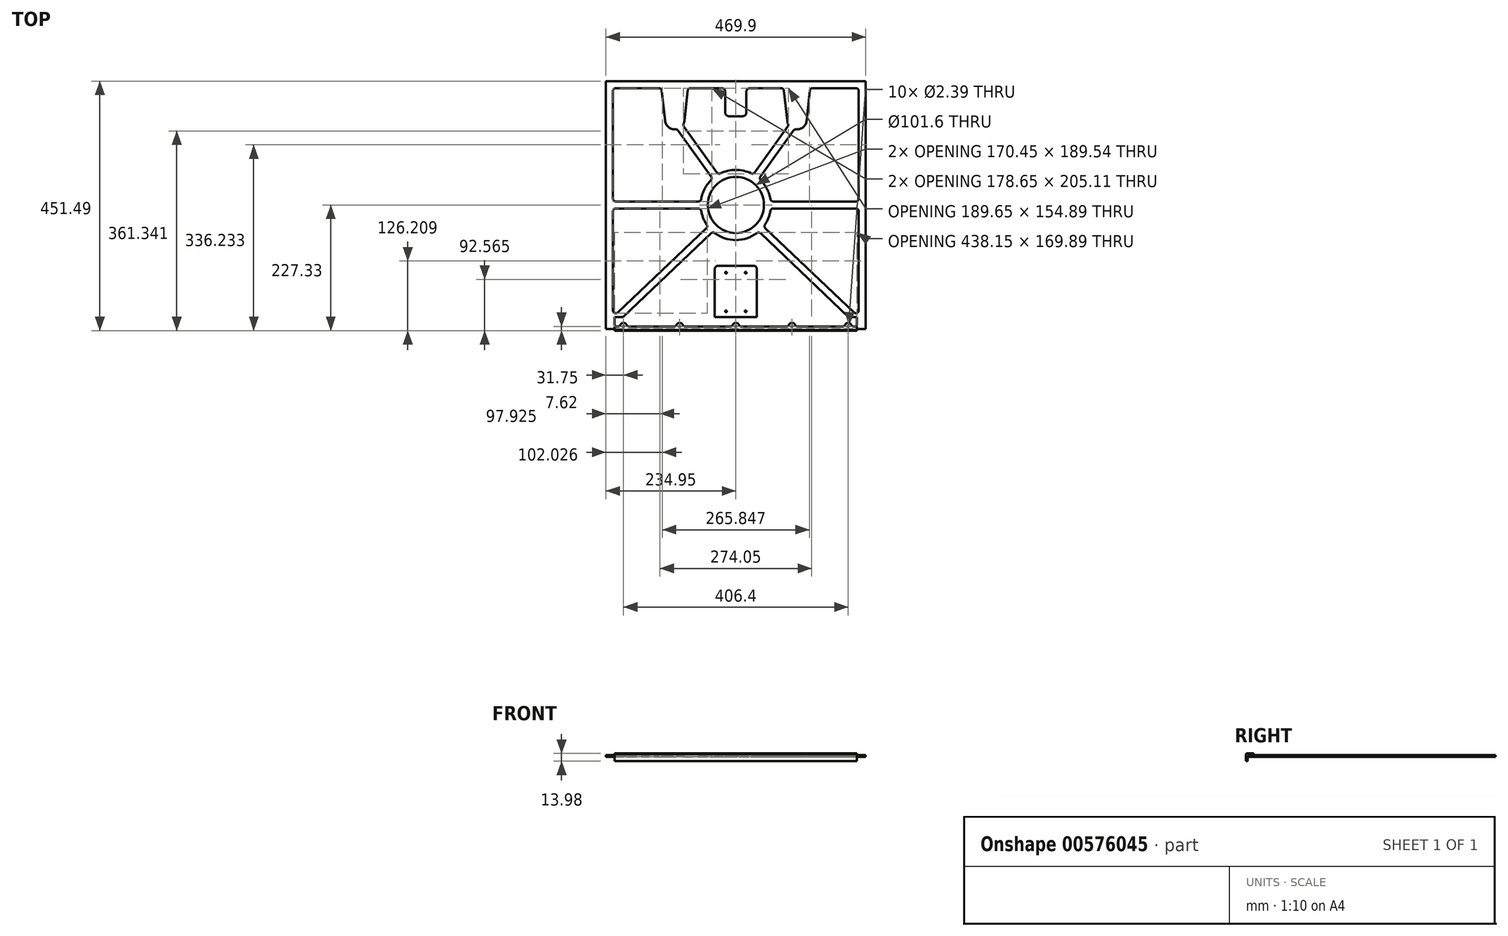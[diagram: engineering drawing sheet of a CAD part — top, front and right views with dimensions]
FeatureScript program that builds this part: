
annotation { "Feature Type Name" : "Feature", "Feature Type Description" : "" }
export const myFeature = defineFeature(function(context is Context, id is Id, definition is map)
    precondition{}
    {
        {
            var Q0;
            Q0=qCreatedBy(makeId("Top.planeOp"),FACE);
            cPlane(context, id + "F0", {"entities" : qUnion([Q0]), "cplaneType" : CPlaneType.OFFSET, "offset" : 3.17 * mm, "width" : 152.4 * mm, "height" : 152.4 * mm});
        }
        {
            var Q0;
            Q0=qCreatedBy(id+"F0.planeOp",FACE);
            var sketch = newSketch(context, id + "F1", { "sketchPlane" : qUnion([Q0])});
            skLineSegment(sketch, "E0.bottom", {"start": v(234.95, -224.15) * mm, "end": v(-234.95, -224.16) * mm});
            skLineSegment(sketch, "E0.top", {"start": v(234.95, 224.16) * mm, "end": v(-234.95, 224.15) * mm});
            skLineSegment(sketch, "E0.left", {"start": v(234.95, -224.15) * mm, "end": v(234.95, 224.16) * mm});
            skLineSegment(sketch, "E0.right", {"start": v(-234.95, -224.16) * mm, "end": v(-234.95, 224.15) * mm});
            skPoint(sketch, "E0.middle", {"position": v(0, 0) * mm});
            skSolve(sketch);
        }
        {
            var Q0;
            Q0=qSketchRegion(id+"F1",true);
            extrude(context, id + "F2", {"entities" : qUnion([Q0]), "depth" : 3.17 * mm, "offsetDistance" : 25.4 * mm});
        }
        {
            var Q0;
            Q0=makeQuery(id+"F2.opExtrude","CAP_FACE",FACE,{"disambiguationData":[OSD([sQuery(id+"F1.wireOp",EDGE,"E0.bottom"),sQuery(id+"F1.wireOp",EDGE,"E0.top"),sQuery(id+"F1.wireOp",EDGE,"E0.left"),sQuery(id+"F1.wireOp",EDGE,"E0.right")])],"isStart":false});
            var sketch = newSketch(context, id + "F3", { "sketchPlane" : qUnion([Q0])});
            skLineSegment(sketch, "E1", {"start": v(-234.95, -224.16) * mm, "end": v(-219.08, -224.16) * mm});
            skLineSegment(sketch, "E2", {"start": v(-219.08, -224.16) * mm, "end": v(-219.08, -249.56) * mm});
            skSolve(sketch);
        }
        {
            var Q0;
            Q0=sQuery(id+"F3.wireOp",EDGE,"E2");
            cPlane(context, id + "F4", {"entities" : qUnion([Q0]), "cplaneType" : CPlaneType.LINE_ANGLE, "offset" : 25.4 * mm, "angle" : 90 * degree, "width" : 152.4 * mm, "height" : 152.4 * mm});
        }
        {
            var Q0;
            Q0=qCreatedBy(id+"F4.planeOp",FACE);
            var sketch = newSketch(context, id + "F5", { "sketchPlane" : qUnion([Q0])});
            skLineSegment(sketch, "E3", {"start": v(-224.16, 6.35) * mm, "end": v(-224.16, 9.52) * mm});
            skLineSegment(sketch, "E4", {"start": v(-224.16, 9.52) * mm, "end": v(-227.33, 9.52) * mm});
            skLineSegment(sketch, "E5", {"start": v(-227.33, 9.52) * mm, "end": v(-208.28, 9.52) * mm});
            skLineSegment(sketch, "E6", {"start": v(-208.28, 9.52) * mm, "end": v(-208.28, 6.35) * mm});
            skLineSegment(sketch, "E7", {"start": v(-208.28, 6.35) * mm, "end": v(-224.16, 6.35) * mm});
            skLineSegment(sketch, "E8", {"start": v(-227.33, 9.52) * mm, "end": v(-227.33, -9.53) * mm});
            skLineSegment(sketch, "E9", {"start": v(-227.33, -9.53) * mm, "end": v(-224.16, -9.53) * mm});
            skLineSegment(sketch, "E10", {"start": v(-224.16, -9.53) * mm, "end": v(-224.16, 6.35) * mm});
            skSolve(sketch);
        }
        {
            var Q0;
            Q0=qSketchRegion(id+"F5",true);
            extrude(context, id + "F6", {"entities" : qUnion([Q0]), "depth" : 438.15 * mm, "offsetDistance" : 25.4 * mm});
        }
        {
            var Q0;
            {var subQ2=sQuery(id+"F3.wireOp",EDGE,"E1");Q0=makeQuery(id+"F3.imprint","IMPRINT",FACE,{"disambiguationData":[TD([[makeQuery(id+"F3.imprint","IMPRINT",EDGE,{"derivedFrom":subQ2}),-1.0]])]});}
            var sketch = newSketch(context, id + "F7", { "sketchPlane" : qUnion([Q0])});
            skLineSegment(sketch, "E11", {"start": v(-234.95, 224.15) * mm, "end": v(-110.5, 224.15) * mm});
            skLineSegment(sketch, "E12", {"start": v(-110.5, 224.15) * mm, "end": v(-110.5, 154.3) * mm});
            skArc(sketch, "E13", {"start": v(-121.74, 153.07) * mm, "mid": v(-110.49, 143) * mm, "end": v(-99.24, 153.07) * mm});
            skLineSegment(sketch, "E14", {"start": v(-110.5, 224.15) * mm, "end": v(-129.54, 224.15) * mm});
            skLineSegment(sketch, "E15", {"start": v(-129.54, 224.15) * mm, "end": v(-121.74, 153.07) * mm});
            skLineSegment(sketch, "E16.MirrorCS", {"start": v(-91.44, 224.15) * mm, "end": v(-99.24, 153.07) * mm});
            skLineSegment(sketch, "E17.MirrorCS", {"start": v(-110.5, 224.15) * mm, "end": v(-91.44, 224.15) * mm});
            skLineSegment(sketch, "E18", {"start": v(-91.44, 224.15) * mm, "end": v(0, 224.15) * mm});
            skLineSegment(sketch, "E19", {"start": v(0, 224.15) * mm, "end": v(0, 261.42) * mm});
            skLineSegment(sketch, "E20.MirrorCS", {"start": v(91.44, 224.15) * mm, "end": v(0, 224.15) * mm});
            skLineSegment(sketch, "E21.MirrorCS", {"start": v(110.5, 224.15) * mm, "end": v(91.44, 224.15) * mm});
            skLineSegment(sketch, "E22.MirrorCS", {"start": v(129.54, 224.15) * mm, "end": v(121.74, 153.07) * mm});
            skLineSegment(sketch, "E23.MirrorCS", {"start": v(91.44, 224.15) * mm, "end": v(99.24, 153.07) * mm});
            skLineSegment(sketch, "E24.MirrorCS", {"start": v(110.5, 224.15) * mm, "end": v(110.5, 154.3) * mm});
            skArc(sketch, "E25.MirrorCS", {"start": v(121.74, 153.07) * mm, "mid": v(110.49, 143) * mm, "end": v(99.24, 153.07) * mm});
            skLineSegment(sketch, "E26.MirrorCS", {"start": v(110.5, 224.15) * mm, "end": v(129.54, 224.15) * mm});
            skLineSegment(sketch, "E27.MirrorCS", {"start": v(234.95, 224.15) * mm, "end": v(110.5, 224.15) * mm});
            skLineSegment(sketch, "E28.bottom", {"start": v(-234.95, 224.15) * mm, "end": v(234.95, 224.15) * mm});
            skLineSegment(sketch, "E28.top", {"start": v(-234.95, -224.15) * mm, "end": v(234.95, -224.15) * mm});
            skLineSegment(sketch, "E28.left", {"start": v(-234.95, 224.15) * mm, "end": v(-234.95, -224.15) * mm});
            skLineSegment(sketch, "E28.right", {"start": v(234.95, 224.15) * mm, "end": v(234.95, -224.15) * mm});
            skLineSegment(sketch, "E29.0", {"start": v(-222.25, 206.37) * mm, "end": v(-222.25, 11.43) * mm});
            skLineSegment(sketch, "E29.1", {"start": v(-217.17, 211.45) * mm, "end": v(-139.09, 211.45) * mm});
            skLineSegment(sketch, "E29.2", {"start": v(222.25, -11.43) * mm, "end": v(222.25, -190.84) * mm});
            skLineSegment(sketch, "E29.3", {"start": v(-200.33, -211.45) * mm, "end": v(-44.45, -211.45) * mm});
            skLineSegment(sketch, "E30.0", {"start": v(-86.94, 206.93) * mm, "end": v(-92.93, 152.38) * mm});
            skArc(sketch, "E30.1", {"start": v(-128.05, 152.38) * mm, "mid": v(-121.64, 140.6) * mm, "end": v(-108.82, 136.72) * mm});
            skLineSegment(sketch, "E30.2", {"start": v(-134.04, 206.93) * mm, "end": v(-128.05, 152.38) * mm});
            skLineSegment(sketch, "E31.0", {"start": v(134.04, 206.93) * mm, "end": v(128.05, 152.38) * mm});
            skArc(sketch, "E31.1", {"start": v(128.05, 152.38) * mm, "mid": v(121.64, 140.6) * mm, "end": v(108.82, 136.72) * mm});
            skLineSegment(sketch, "E31.2", {"start": v(86.94, 206.93) * mm, "end": v(92.93, 152.38) * mm});
            skCircle(sketch, "E32", {"center": v(0, 0) * mm, "radius": 50.8 * mm});
            skArc(sketch, "E33.0", {"start": v(-62.61, -10.58) * mm, "mid": v(-58.96, -23.57) * mm, "end": v(-52.66, -35.5) * mm});
            skLineSegment(sketch, "E34.0", {"start": v(-34.2, 58.68) * mm, "end": v(-93.88, 142.01) * mm});
            skLineSegment(sketch, "E35.0", {"start": v(-44.61, -51.21) * mm, "end": v(-203.83, -202.7) * mm});
            skLineSegment(sketch, "E36.trimOffspring", {"start": v(-44.53, 51.28) * mm, "end": v(-104.2, 134.62) * mm});
            skLineSegment(sketch, "E37.trimOffspring", {"start": v(-67.62, 6.35) * mm, "end": v(-217.17, 6.35) * mm});
            skLineSegment(sketch, "E38.trimOffspring", {"start": v(-67.62, -6.35) * mm, "end": v(-217.17, -6.35) * mm});
            skLineSegment(sketch, "E39.trimOffspring", {"start": v(-53.37, -42.01) * mm, "end": v(-213.67, -194.53) * mm});
            skLineSegment(sketch, "E40.trimOffspring", {"start": v(-36.8, -35.02) * mm, "end": v(-222.25, -211.45) * mm});
            skLineSegment(sketch, "E41.trimOffspring", {"start": v(-50.8, 0) * mm, "end": v(-222.25, 0) * mm});
            skLineSegment(sketch, "E42.trimOffspring", {"start": v(-29.58, 41.3) * mm, "end": v(-103.9, 145.1) * mm});
            skLineSegment(sketch, "E43.MirrorCS", {"start": v(34.2, 58.68) * mm, "end": v(93.88, 142.01) * mm});
            skLineSegment(sketch, "E44.MirrorCS", {"start": v(29.58, 41.3) * mm, "end": v(103.9, 145.1) * mm});
            skLineSegment(sketch, "E45.MirrorCS", {"start": v(44.53, 51.28) * mm, "end": v(104.2, 134.62) * mm});
            skLineSegment(sketch, "E46.MirrorCS", {"start": v(67.62, 6.35) * mm, "end": v(217.17, 6.35) * mm});
            skLineSegment(sketch, "E47.MirrorCS", {"start": v(50.8, 0) * mm, "end": v(222.25, 0) * mm});
            skLineSegment(sketch, "E48.MirrorCS", {"start": v(67.62, -6.35) * mm, "end": v(217.17, -6.35) * mm});
            skLineSegment(sketch, "E49.MirrorCS", {"start": v(53.37, -42.01) * mm, "end": v(213.67, -194.53) * mm});
            skLineSegment(sketch, "E50.MirrorCS", {"start": v(36.8, -35.02) * mm, "end": v(222.25, -211.45) * mm});
            skLineSegment(sketch, "E51.MirrorCS", {"start": v(44.61, -51.21) * mm, "end": v(203.83, -202.7) * mm});
            skArc(sketch, "E52.filletArc", {"start": v(-134.04, 206.93) * mm, "mid": v(-135.7, 210.16) * mm, "end": v(-139.09, 211.45) * mm});
            skPoint(sketch, "E53.visualSharp", {"position": v(-222.25, 211.45) * mm});
            skArc(sketch, "E53.filletArc", {"start": v(-217.17, 211.45) * mm, "mid": v(-220.76, 209.97) * mm, "end": v(-222.25, 206.37) * mm});
            skPoint(sketch, "E54.newPointA", {"position": v(-222.25, -211.45) * mm});
            skPoint(sketch, "E54.newPointB", {"position": v(-222.25, 6.35) * mm});
            skArc(sketch, "E54.filletArc", {"start": v(-222.25, 11.43) * mm, "mid": v(-220.76, 7.84) * mm, "end": v(-217.17, 6.35) * mm});
            skLineSegment(sketch, "E55", {"start": v(217.17, 211.45) * mm, "end": v(139.09, 211.45) * mm});
            skLineSegment(sketch, "E56", {"start": v(-222.25, -11.43) * mm, "end": v(-222.25, -190.84) * mm});
            skArc(sketch, "E57.trimOffspring", {"start": v(-38.07, -50.83) * mm, "mid": v(0, -63.5) * mm, "end": v(38.07, -50.83) * mm});
            skArc(sketch, "E58.trimOffspring", {"start": v(52.66, -35.5) * mm, "mid": v(58.96, -23.57) * mm, "end": v(62.61, -10.58) * mm});
            skArc(sketch, "E59.trimOffspring", {"start": v(62.61, 10.58) * mm, "mid": v(56.48, 29.02) * mm, "end": v(45.06, 44.75) * mm});
            skArc(sketch, "E60.trimOffspring", {"start": v(27.85, 57.07) * mm, "mid": v(0, 63.5) * mm, "end": v(-27.85, 57.07) * mm});
            skArc(sketch, "E61.trimOffspring", {"start": v(-45.06, 44.75) * mm, "mid": v(-56.48, 29.02) * mm, "end": v(-62.61, 10.58) * mm});
            skPoint(sketch, "E62.orphan", {"position": v(-110.2, 143) * mm});
            skPoint(sketch, "E63.orphan", {"position": v(-99.88, 150.39) * mm});
            skArc(sketch, "E64.trimOffspring", {"start": v(-94.38, 147.06) * mm, "mid": v(-93.45, 149.66) * mm, "end": v(-92.93, 152.38) * mm});
            skPoint(sketch, "E65.orphan", {"position": v(99.88, 150.39) * mm});
            skPoint(sketch, "E66.orphan", {"position": v(110.2, 143) * mm});
            skArc(sketch, "E67.trimOffspring", {"start": v(94.38, 147.06) * mm, "mid": v(93.45, 149.66) * mm, "end": v(92.93, 152.38) * mm});
            skPoint(sketch, "E68.visualSharp", {"position": v(-106.06, 137.2) * mm});
            skArc(sketch, "E68.filletArc", {"start": v(-104.2, 134.62) * mm, "mid": v(-106.23, 136.29) * mm, "end": v(-108.82, 136.72) * mm});
            skPoint(sketch, "E69.newPointA", {"position": v(-34.5, 37.28) * mm});
            skArc(sketch, "E69.filletArc", {"start": v(-45.06, 44.75) * mm, "mid": v(-43.6, 47.92) * mm, "end": v(-44.53, 51.28) * mm});
            skPoint(sketch, "E70.newPointB", {"position": v(-50.4, 6.35) * mm});
            skArc(sketch, "E70.filletArc", {"start": v(-67.62, 6.35) * mm, "mid": v(-64.34, 7.55) * mm, "end": v(-62.61, 10.58) * mm});
            skPoint(sketch, "E71.newPointA", {"position": v(-50.4, -6.35) * mm});
            skArc(sketch, "E71.filletArc", {"start": v(-62.61, -10.58) * mm, "mid": v(-64.34, -7.55) * mm, "end": v(-67.62, -6.35) * mm});
            skPoint(sketch, "E72.newPointB", {"position": v(-40.9, -30.14) * mm});
            skArc(sketch, "E72.filletArc", {"start": v(-53.37, -42.01) * mm, "mid": v(-51.82, -38.88) * mm, "end": v(-52.66, -35.5) * mm});
            skPoint(sketch, "E73.newPointA", {"position": v(-222.25, -202.7) * mm});
            skArc(sketch, "E73.filletArc", {"start": v(-222.25, -190.84) * mm, "mid": v(-219.17, -195.51) * mm, "end": v(-213.67, -194.53) * mm});
            skPoint(sketch, "E74.visualSharp", {"position": v(-222.25, -6.35) * mm});
            skArc(sketch, "E74.filletArc", {"start": v(-217.17, -6.35) * mm, "mid": v(-220.76, -7.84) * mm, "end": v(-222.25, -11.43) * mm});
            skPoint(sketch, "E75.newPointB", {"position": v(-32.14, -39.34) * mm});
            skArc(sketch, "E75.filletArc", {"start": v(-38.07, -50.83) * mm, "mid": v(-41.41, -49.82) * mm, "end": v(-44.61, -51.21) * mm});
            skPoint(sketch, "E76.newPointB", {"position": v(32.14, -39.34) * mm});
            skArc(sketch, "E76.filletArc", {"start": v(44.61, -51.21) * mm, "mid": v(41.41, -49.82) * mm, "end": v(38.07, -50.83) * mm});
            skPoint(sketch, "E77.newPointA", {"position": v(213.04, -211.46) * mm});
            skArc(sketch, "E77.filletArc", {"start": v(200.33, -211.45) * mm, "mid": v(205.05, -208.26) * mm, "end": v(203.83, -202.7) * mm});
            skPoint(sketch, "E78.newPointB", {"position": v(-213.04, -211.46) * mm});
            skArc(sketch, "E78.filletArc", {"start": v(-203.83, -202.7) * mm, "mid": v(-205.05, -208.26) * mm, "end": v(-200.33, -211.46) * mm});
            skPoint(sketch, "E79.newPointA", {"position": v(222.25, -202.7) * mm});
            skArc(sketch, "E79.filletArc", {"start": v(213.67, -194.53) * mm, "mid": v(219.17, -195.51) * mm, "end": v(222.25, -190.84) * mm});
            skPoint(sketch, "E80.newPointB", {"position": v(222.25, -6.35) * mm});
            skArc(sketch, "E80.filletArc", {"start": v(222.25, -11.43) * mm, "mid": v(220.76, -7.84) * mm, "end": v(217.17, -6.35) * mm});
            skPoint(sketch, "E81.newPointA", {"position": v(50.4, -6.35) * mm});
            skArc(sketch, "E81.filletArc", {"start": v(67.62, -6.35) * mm, "mid": v(64.34, -7.55) * mm, "end": v(62.61, -10.58) * mm});
            skPoint(sketch, "E82.newPointA", {"position": v(40.9, -30.14) * mm});
            skArc(sketch, "E82.filletArc", {"start": v(52.66, -35.5) * mm, "mid": v(51.82, -38.88) * mm, "end": v(53.37, -42.01) * mm});
            skLineSegment(sketch, "E83", {"start": v(222.25, 206.37) * mm, "end": v(222.25, 11.43) * mm});
            skPoint(sketch, "E84.visualSharp", {"position": v(222.25, 6.35) * mm});
            skArc(sketch, "E84.filletArc", {"start": v(217.17, 6.35) * mm, "mid": v(220.76, 7.84) * mm, "end": v(222.25, 11.43) * mm});
            skPoint(sketch, "E85.visualSharp", {"position": v(222.25, 211.45) * mm});
            skArc(sketch, "E85.filletArc", {"start": v(222.25, 206.37) * mm, "mid": v(220.76, 209.97) * mm, "end": v(217.17, 211.45) * mm});
            skArc(sketch, "E86.filletArc", {"start": v(139.09, 211.45) * mm, "mid": v(135.7, 210.16) * mm, "end": v(134.04, 206.93) * mm});
            skPoint(sketch, "E87.visualSharp", {"position": v(106.06, 137.2) * mm});
            skArc(sketch, "E87.filletArc", {"start": v(108.82, 136.72) * mm, "mid": v(106.23, 136.29) * mm, "end": v(104.2, 134.62) * mm});
            skPoint(sketch, "E88.newPointA", {"position": v(34.5, 37.28) * mm});
            skArc(sketch, "E88.filletArc", {"start": v(44.53, 51.28) * mm, "mid": v(43.6, 47.92) * mm, "end": v(45.06, 44.75) * mm});
            skPoint(sketch, "E89.newPointB", {"position": v(50.4, 6.35) * mm});
            skArc(sketch, "E89.filletArc", {"start": v(62.61, 10.58) * mm, "mid": v(64.34, 7.55) * mm, "end": v(67.62, 6.35) * mm});
            skLineSegment(sketch, "E90", {"start": v(110.5, 224.15) * mm, "end": v(110.5, 211.46) * mm});
            skLineSegment(sketch, "E91", {"start": v(81.9, 211.46) * mm, "end": v(25.4, 211.46) * mm});
            skArc(sketch, "E92.filletArc", {"start": v(-81.9, 211.46) * mm, "mid": v(-85.28, 210.16) * mm, "end": v(-86.94, 206.93) * mm});
            skArc(sketch, "E93.filletArc", {"start": v(86.94, 206.93) * mm, "mid": v(85.28, 210.16) * mm, "end": v(81.9, 211.46) * mm});
            skPoint(sketch, "E94.visualSharp", {"position": v(95.73, 144.6) * mm});
            skArc(sketch, "E94.filletArc", {"start": v(93.88, 142.01) * mm, "mid": v(94.8, 144.47) * mm, "end": v(94.38, 147.06) * mm});
            skPoint(sketch, "E95.newPointA", {"position": v(24.18, 44.68) * mm});
            skArc(sketch, "E95.filletArc", {"start": v(27.85, 57.07) * mm, "mid": v(31.32, 56.7) * mm, "end": v(34.2, 58.68) * mm});
            skPoint(sketch, "E96.newPointB", {"position": v(-24.18, 44.68) * mm});
            skArc(sketch, "E96.filletArc", {"start": v(-34.2, 58.68) * mm, "mid": v(-31.32, 56.7) * mm, "end": v(-27.85, 57.07) * mm});
            skPoint(sketch, "E97.visualSharp", {"position": v(-95.73, 144.6) * mm});
            skArc(sketch, "E97.filletArc", {"start": v(-94.38, 147.06) * mm, "mid": v(-94.8, 144.47) * mm, "end": v(-93.88, 142.01) * mm});
            skLineSegment(sketch, "E98", {"start": v(-19.05, 205.1) * mm, "end": v(-19.05, 167) * mm});
            skLineSegment(sketch, "E99", {"start": v(-12.7, 160.66) * mm, "end": v(12.7, 160.66) * mm});
            skLineSegment(sketch, "E100", {"start": v(19.05, 167) * mm, "end": v(19.05, 205.1) * mm});
            skLineSegment(sketch, "E101.trimOffspring", {"start": v(-25.4, 211.46) * mm, "end": v(-81.9, 211.46) * mm});
            skPoint(sketch, "E102.start.orphan", {"position": v(0, 211.46) * mm});
            skPoint(sketch, "E103.visualSharp", {"position": v(-19.05, 211.46) * mm});
            skArc(sketch, "E103.filletArc", {"start": v(-19.05, 205.1) * mm, "mid": v(-20.9, 209.6) * mm, "end": v(-25.4, 211.46) * mm});
            skPoint(sketch, "E104.visualSharp", {"position": v(19.05, 211.46) * mm});
            skArc(sketch, "E104.filletArc", {"start": v(25.4, 211.46) * mm, "mid": v(20.9, 209.6) * mm, "end": v(19.05, 205.1) * mm});
            skPoint(sketch, "E105.visualSharp", {"position": v(19.05, 160.66) * mm});
            skArc(sketch, "E105.filletArc", {"start": v(12.7, 160.66) * mm, "mid": v(17.2, 162.51) * mm, "end": v(19.05, 167) * mm});
            skPoint(sketch, "E106.visualSharp", {"position": v(-19.05, 160.66) * mm});
            skArc(sketch, "E106.filletArc", {"start": v(-19.05, 167) * mm, "mid": v(-17.2, 162.51) * mm, "end": v(-12.7, 160.66) * mm});
            skLineSegment(sketch, "E107", {"start": v(0, -211.45) * mm, "end": v(0, -109.86) * mm});
            skLineSegment(sketch, "E108", {"start": v(0, -109.86) * mm, "end": v(-31.75, -109.86) * mm});
            skLineSegment(sketch, "E109", {"start": v(-38.1, -116.2) * mm, "end": v(-38.1, -205.1) * mm});
            skLineSegment(sketch, "E110.MirrorCS", {"start": v(0, -109.86) * mm, "end": v(31.75, -109.86) * mm});
            skLineSegment(sketch, "E111.MirrorCS", {"start": v(38.1, -116.2) * mm, "end": v(38.1, -205.1) * mm});
            skLineSegment(sketch, "E112.trimOffspring", {"start": v(44.45, -211.45) * mm, "end": v(200.33, -211.45) * mm});
            skPoint(sketch, "E113.visualSharp", {"position": v(-38.1, -109.86) * mm});
            skArc(sketch, "E113.filletArc", {"start": v(-31.75, -109.86) * mm, "mid": v(-36.24, -111.71) * mm, "end": v(-38.1, -116.2) * mm});
            skPoint(sketch, "E114.visualSharp", {"position": v(38.1, -109.86) * mm});
            skArc(sketch, "E114.filletArc", {"start": v(38.1, -116.2) * mm, "mid": v(36.24, -111.71) * mm, "end": v(31.75, -109.86) * mm});
            skPoint(sketch, "E115.visualSharp", {"position": v(-38.1, -211.45) * mm});
            skArc(sketch, "E115.filletArc", {"start": v(-44.45, -211.45) * mm, "mid": v(-39.96, -209.6) * mm, "end": v(-38.1, -205.1) * mm});
            skPoint(sketch, "E116.visualSharp", {"position": v(38.1, -211.46) * mm});
            skArc(sketch, "E116.filletArc", {"start": v(38.1, -205.1) * mm, "mid": v(39.96, -209.6) * mm, "end": v(44.45, -211.46) * mm});
            skSolve(sketch);
        }
        {
            var Q0;
            Q0=makeQuery(id+"F7.imprint","IMPRINT",FACE,{"disambiguationData":[TD([[makeQuery(id+"F7.imprint","IMPRINT",EDGE,{"derivedFrom":sQuery(id+"F7.wireOp",EDGE,"E30.0")}),1.0]])]});
            var Q1;
            Q1=makeQuery(id+"F7.imprint","IMPRINT",FACE,{"disambiguationData":[TD([[makeQuery(id+"F7.imprint","IMPRINT",EDGE,{"derivedFrom":sQuery(id+"F7.wireOp",EDGE,"E31.0")}),1.0]])]});
            var Q2;
            {var subQ0=sQuery(id+"F7.wireOp",EDGE,"E32");var subQ1=makeQuery(id+"F7.imprint","IMPRINT",VERTEX,{"disambiguationData":[OD(0.0)],"derivedFrom":subQ0});Q2=makeQuery(id+"F7.imprint","IMPRINT",FACE,{"disambiguationData":[TD([[makeQuery(id+"F7.imprint","IMPRINT",EDGE,{"disambiguationData":[TD([[subQ1,1.0]])],"derivedFrom":subQ0}),1.0]])]});}
            var Q3;
            Q3=makeQuery(id+"F7.imprint","IMPRINT",FACE,{"disambiguationData":[TD([[makeQuery(id+"F7.imprint","IMPRINT",EDGE,{"derivedFrom":sQuery(id+"F7.wireOp",EDGE,"E29.2")}),-1.0]])]});
            var Q4;
            Q4=makeQuery(id+"F7.imprint","IMPRINT",FACE,{"disambiguationData":[TD([[makeQuery(id+"F7.imprint","IMPRINT",EDGE,{"derivedFrom":sQuery(id+"F7.wireOp",EDGE,"E29.3")}),1.0]])]});
            var Q5;
            Q5=makeQuery(id+"F7.imprint","IMPRINT",FACE,{"disambiguationData":[TD([[makeQuery(id+"F7.imprint","IMPRINT",EDGE,{"derivedFrom":sQuery(id+"F7.wireOp",EDGE,"E33.0")}),-1.0]])]});
            var Q6;
            Q6=makeQuery(id+"F7.imprint","IMPRINT",FACE,{"disambiguationData":[TD([[makeQuery(id+"F7.imprint","IMPRINT",EDGE,{"derivedFrom":sQuery(id+"F7.wireOp",EDGE,"E29.0")}),1.0]])]});
            extrude(context, id + "F8", {"entities" : qUnion([Q0, Q1, Q2, Q3, Q4, Q5, Q6]), "operationType" : NewBodyOperationType.REMOVE, "oppositeDirection" : true, "depth" : 25.4 * mm, "offsetDistance" : 25.4 * mm});
        }
        {
            var Q0;
            {var subQ2=sQuery(id+"F3.wireOp",EDGE,"E1");Q0=makeQuery(id+"F3.imprint","IMPRINT",FACE,{"disambiguationData":[TD([[makeQuery(id+"F3.imprint","IMPRINT",EDGE,{"derivedFrom":subQ2}),-1.0]])]});}
            var sketch = newSketch(context, id + "F9", { "sketchPlane" : qUnion([Q0])});
            skLineSegment(sketch, "E117", {"start": v(0, -122.55) * mm, "end": v(0, -192.4) * mm});
            skLineSegment(sketch, "E118", {"start": v(-17.78, -192.4) * mm, "end": v(17.78, -192.4) * mm});
            skLineSegment(sketch, "E119", {"start": v(-17.78, -122.55) * mm, "end": v(17.78, -122.55) * mm});
            skLineSegment(sketch, "E120", {"start": v(0, -192.4) * mm, "end": v(0, -224.16) * mm});
            skSolve(sketch);
        }
        {
            var Q0;
            Q0=sQuery(id+"F9.wireOp",VERTEX,"E119.start");
            var Q1;
            Q1=sQuery(id+"F9.wireOp",VERTEX,"E119.end");
            var Q2;
            Q2=sQuery(id+"F9.wireOp",VERTEX,"E118.end");
            var Q3;
            Q3=sQuery(id+"F9.wireOp",VERTEX,"E118.start");
            var Q4;
            Q4=makeQuery(id+"F2.opExtrude","SWEPT_BODY",BODY,{"disambiguationData":[OSD([sQuery(id+"F1.wireOp",EDGE,"E0.bottom"),sQuery(id+"F1.wireOp",EDGE,"E0.top"),sQuery(id+"F1.wireOp",EDGE,"E0.left"),sQuery(id+"F1.wireOp",EDGE,"E0.right")])]});
            hole(context, id + "F10", {"style" : HoleStyle.SIMPLE, "endStyle" : HoleEndStyle.BLIND, "standardTappedOrClearance" : lookupTablePath({ "fit" : "Close (ASME)", "standard" : "ANSI", "size" : "#4", "type" : "Clearance" }), "standardBlindInLast" : lookupTablePath({ "fit" : "Close", "standard" : "ANSI", "size" : "#4", "type" : "Clearance" }), "holeDiameter" : 3.05 * mm, "majorDiameter" : 6.35 * mm, "holeDepth" : 25.4 * mm, "isTappedThrough" : true, "tappedDepth" : 12.7 * mm, "tapClearance" : 3, "locations" : qUnion([Q0, Q1, Q2, Q3]), "scope" : qUnion([Q4])});
        }
        {
            var Q0;
            Q0=makeQuery(id+"F6.opExtrude","SWEPT_FACE",FACE,{"disambiguationData":[OSD([sQuery(id+"F5.wireOp",EDGE,"E5")])]});
            var sketch = newSketch(context, id + "F11", { "sketchPlane" : qUnion([Q0])});
            skLineSegment(sketch, "E121", {"start": v(-219.08, -227.33) * mm, "end": v(219.08, -227.33) * mm});
            skLineSegment(sketch, "E122", {"start": v(0, -227.33) * mm, "end": v(0, -219.71) * mm});
            skLineSegment(sketch, "E123", {"start": v(0, -227.33) * mm, "end": v(-101.6, -227.33) * mm});
            skLineSegment(sketch, "E124", {"start": v(-101.6, -227.33) * mm, "end": v(-203.2, -227.33) * mm});
            skLineSegment(sketch, "E125", {"start": v(-101.6, -227.33) * mm, "end": v(-101.6, -219.71) * mm});
            skLineSegment(sketch, "E126", {"start": v(-203.2, -227.33) * mm, "end": v(-203.2, -219.71) * mm});
            skCircle(sketch, "E127", {"center": v(-203.2, -219.71) * mm, "radius": 6.35 * mm});
            skCircle(sketch, "E128", {"center": v(-101.6, -219.71) * mm, "radius": 6.35 * mm});
            skCircle(sketch, "E129", {"center": v(0, -219.71) * mm, "radius": 6.35 * mm});
            skLineSegment(sketch, "E130.0", {"start": v(-219.08, -219.71) * mm, "end": v(219.08, -219.71) * mm});
            skLineSegment(sketch, "E131", {"start": v(-219.08, -219.71) * mm, "end": v(-219.08, -202.94) * mm});
            skLineSegment(sketch, "E132", {"start": v(-219.08, -202.94) * mm, "end": v(0, -202.94) * mm});
            skLineSegment(sketch, "E133.MirrorCS", {"start": v(219.08, -219.71) * mm, "end": v(219.08, -202.94) * mm});
            skCircle(sketch, "E134.MirrorC", {"center": v(101.6, -219.71) * mm, "radius": 6.35 * mm});
            skLineSegment(sketch, "E135.MirrorCS", {"start": v(219.08, -202.94) * mm, "end": v(0, -202.94) * mm});
            skLineSegment(sketch, "E136.MirrorCS", {"start": v(101.6, -227.33) * mm, "end": v(203.2, -227.33) * mm});
            skLineSegment(sketch, "E137.MirrorCS", {"start": v(203.2, -227.33) * mm, "end": v(203.2, -219.71) * mm});
            skLineSegment(sketch, "E138.MirrorCS", {"start": v(0, -227.33) * mm, "end": v(101.6, -227.33) * mm});
            skLineSegment(sketch, "E139.MirrorCS", {"start": v(101.6, -227.33) * mm, "end": v(101.6, -219.71) * mm});
            skCircle(sketch, "E140.MirrorC", {"center": v(203.2, -219.71) * mm, "radius": 6.35 * mm});
            skSolve(sketch);
        }
        {
            var Q0;
            {var subQ0=sQuery(id+"F11.wireOp",EDGE,"E132");Q0=makeQuery(id+"F11.imprint","IMPRINT",FACE,{"disambiguationData":[TD([[makeQuery(id+"F11.imprint","IMPRINT",EDGE,{"derivedFrom":subQ0}),-1.0]])]});}
            var Q1;
            {var subQ2=sQuery(id+"F5.wireOp",EDGE,"E5");var subQ13=makeQuery(id+"F6.opExtrude","SWEPT_EDGE",EDGE,{"disambiguationData":[OSD([subQ2,sQuery(id+"F5.wireOp",EDGE,"E6")])]});Q1=makeQuery(id+"F11.imprint","IMPRINT",FACE,{"disambiguationData":[TD([[makeQuery(id+"F11.imprint","IMPRINT",EDGE,{"derivedFrom":subQ13}),1.0]])]});}
            extrude(context, id + "F12", {"entities" : qUnion([Q0, Q1]), "operationType" : NewBodyOperationType.REMOVE, "oppositeDirection" : true, "depth" : 25.4 * mm, "offsetDistance" : 25.4 * mm});
        }
        {
            var Q0;
            Q0=sQuery(id+"F11.wireOp",VERTEX,"E126.end");
            var Q1;
            Q1=sQuery(id+"F11.wireOp",VERTEX,"E125.end");
            var Q2;
            Q2=sQuery(id+"F11.wireOp",VERTEX,"E122.end");
            var Q3;
            Q3=sQuery(id+"F11.wireOp",VERTEX,"E139.MirrorCS.end");
            var Q4;
            Q4=sQuery(id+"F11.wireOp",VERTEX,"E137.MirrorCS.end");
            var Q5;
            Q5=makeQuery(id+"F2.opExtrude","SWEPT_BODY",BODY,{"disambiguationData":[OSD([sQuery(id+"F1.wireOp",EDGE,"E0.bottom"),sQuery(id+"F1.wireOp",EDGE,"E0.top"),sQuery(id+"F1.wireOp",EDGE,"E0.left"),sQuery(id+"F1.wireOp",EDGE,"E0.right")])]});
            var Q6;
            Q6=makeQuery(id+"F6.opExtrude","SWEPT_BODY",BODY,{"disambiguationData":[OSD([sQuery(id+"F5.wireOp",EDGE,"E5"),sQuery(id+"F5.wireOp",EDGE,"E6"),sQuery(id+"F5.wireOp",EDGE,"E7"),sQuery(id+"F5.wireOp",EDGE,"E8"),sQuery(id+"F5.wireOp",EDGE,"E9"),sQuery(id+"F5.wireOp",EDGE,"E10")])]});
            hole(context, id + "F13", {"style" : HoleStyle.SIMPLE, "endStyle" : HoleEndStyle.BLIND, "standardTappedOrClearance" : lookupTablePath({ "fit" : "Close (ASME)", "standard" : "ANSI", "size" : "#2", "type" : "Clearance" }), "standardBlindInLast" : lookupTablePath({ "fit" : "Close", "standard" : "ANSI", "size" : "#2", "type" : "Clearance" }), "holeDiameter" : 2.4 * mm, "majorDiameter" : 6.35 * mm, "holeDepth" : 25.4 * mm, "isTappedThrough" : true, "tappedDepth" : 12.7 * mm, "tapClearance" : 3, "locations" : qUnion([Q0, Q1, Q2, Q3, Q4]), "scope" : qUnion([Q5, Q6])});
        }
        {
            var Q0;
            {var subQ0=sQuery(id+"F11.wireOp",EDGE,"E140.MirrorC");var subQ1=sQuery(id+"F11.wireOp",EDGE,"E130.0");Q0=makeQuery(id+"F12.boolean.opBoolean","COPY",EDGE,{"derivedFrom":makeQuery(id+"F12.opExtrude","SWEPT_EDGE",EDGE,{"disambiguationData":[OSD([subQ1,subQ0]),TDD([makeQuery(id+"F11.imprint","INTERSECT",VERTEX,{"disambiguationData":[OD(1.0)],"derivedFrom":[subQ1,subQ0]})])]})});}
            var Q1;
            {var subQ0=sQuery(id+"F11.wireOp",EDGE,"E140.MirrorC");var subQ1=sQuery(id+"F11.wireOp",EDGE,"E130.0");Q1=makeQuery(id+"F12.boolean.opBoolean","COPY",EDGE,{"derivedFrom":makeQuery(id+"F12.opExtrude","SWEPT_EDGE",EDGE,{"disambiguationData":[OSD([subQ1,subQ0]),TDD([makeQuery(id+"F11.imprint","INTERSECT",VERTEX,{"disambiguationData":[OD(0.0)],"derivedFrom":[subQ1,subQ0]})])]})});}
            var Q2;
            {var subQ0=sQuery(id+"F11.wireOp",EDGE,"E134.MirrorC");var subQ1=sQuery(id+"F11.wireOp",EDGE,"E130.0");Q2=makeQuery(id+"F12.boolean.opBoolean","COPY",EDGE,{"derivedFrom":makeQuery(id+"F12.opExtrude","SWEPT_EDGE",EDGE,{"disambiguationData":[OSD([subQ1,subQ0]),TDD([makeQuery(id+"F11.imprint","INTERSECT",VERTEX,{"disambiguationData":[OD(0.0)],"derivedFrom":[subQ1,subQ0]})])]})});}
            var Q3;
            {var subQ0=sQuery(id+"F11.wireOp",EDGE,"E129");var subQ1=sQuery(id+"F11.wireOp",EDGE,"E130.0");Q3=makeQuery(id+"F12.boolean.opBoolean","COPY",EDGE,{"derivedFrom":makeQuery(id+"F12.opExtrude","SWEPT_EDGE",EDGE,{"disambiguationData":[OSD([subQ1,subQ0]),TDD([makeQuery(id+"F11.imprint","INTERSECT",VERTEX,{"disambiguationData":[OD(0.0)],"derivedFrom":[subQ1,subQ0]})])]})});}
            var Q4;
            {var subQ0=sQuery(id+"F11.wireOp",EDGE,"E129");var subQ1=sQuery(id+"F11.wireOp",EDGE,"E130.0");Q4=makeQuery(id+"F12.boolean.opBoolean","COPY",EDGE,{"derivedFrom":makeQuery(id+"F12.opExtrude","SWEPT_EDGE",EDGE,{"disambiguationData":[OSD([subQ1,subQ0]),TDD([makeQuery(id+"F11.imprint","INTERSECT",VERTEX,{"disambiguationData":[OD(1.0)],"derivedFrom":[subQ1,subQ0]})])]})});}
            var Q5;
            {var subQ0=sQuery(id+"F11.wireOp",EDGE,"E134.MirrorC");var subQ1=sQuery(id+"F11.wireOp",EDGE,"E130.0");Q5=makeQuery(id+"F12.boolean.opBoolean","COPY",EDGE,{"derivedFrom":makeQuery(id+"F12.opExtrude","SWEPT_EDGE",EDGE,{"disambiguationData":[OSD([subQ1,subQ0]),TDD([makeQuery(id+"F11.imprint","INTERSECT",VERTEX,{"disambiguationData":[OD(1.0)],"derivedFrom":[subQ1,subQ0]})])]})});}
            var Q6;
            {var subQ0=sQuery(id+"F11.wireOp",EDGE,"E130.0");var subQ1=sQuery(id+"F11.wireOp",EDGE,"E128");Q6=makeQuery(id+"F12.boolean.opBoolean","COPY",EDGE,{"derivedFrom":makeQuery(id+"F12.opExtrude","SWEPT_EDGE",EDGE,{"disambiguationData":[OSD([subQ1,subQ0]),TDD([makeQuery(id+"F11.imprint","INTERSECT",VERTEX,{"disambiguationData":[OD(1.0)],"derivedFrom":[subQ1,subQ0]})])]})});}
            var Q7;
            {var subQ0=sQuery(id+"F11.wireOp",EDGE,"E130.0");var subQ1=sQuery(id+"F11.wireOp",EDGE,"E127");Q7=makeQuery(id+"F12.boolean.opBoolean","COPY",EDGE,{"derivedFrom":makeQuery(id+"F12.opExtrude","SWEPT_EDGE",EDGE,{"disambiguationData":[OSD([subQ1,subQ0]),TDD([makeQuery(id+"F11.imprint","INTERSECT",VERTEX,{"disambiguationData":[OD(1.0)],"derivedFrom":[subQ1,subQ0]})])]})});}
            var Q8;
            {var subQ0=sQuery(id+"F11.wireOp",EDGE,"E130.0");var subQ1=sQuery(id+"F11.wireOp",EDGE,"E128");Q8=makeQuery(id+"F12.boolean.opBoolean","COPY",EDGE,{"derivedFrom":makeQuery(id+"F12.opExtrude","SWEPT_EDGE",EDGE,{"disambiguationData":[OSD([subQ1,subQ0]),TDD([makeQuery(id+"F11.imprint","INTERSECT",VERTEX,{"disambiguationData":[OD(0.0)],"derivedFrom":[subQ1,subQ0]})])]})});}
            var Q9;
            {var subQ0=sQuery(id+"F11.wireOp",EDGE,"E130.0");var subQ1=sQuery(id+"F11.wireOp",EDGE,"E127");Q9=makeQuery(id+"F12.boolean.opBoolean","COPY",EDGE,{"derivedFrom":makeQuery(id+"F12.opExtrude","SWEPT_EDGE",EDGE,{"disambiguationData":[OSD([subQ1,subQ0]),TDD([makeQuery(id+"F11.imprint","INTERSECT",VERTEX,{"disambiguationData":[OD(0.0)],"derivedFrom":[subQ1,subQ0]})])]})});}
            var Q10;
            Q10=makeQuery(id+"F12.boolean.opBoolean","COPY",EDGE,{"derivedFrom":makeQuery(id+"F12.opExtrude","SWEPT_EDGE",EDGE,{"disambiguationData":[OSD([sQuery(id+"F5.wireOp",EDGE,"E5"),sQuery(id+"F11.wireOp",EDGE,"E130.0"),sQuery(id+"F11.wireOp",EDGE,"E131")])]})});
            var Q11;
            Q11=makeQuery(id+"F12.boolean.opBoolean","COPY",EDGE,{"derivedFrom":makeQuery(id+"F12.opExtrude","SWEPT_EDGE",EDGE,{"disambiguationData":[OSD([sQuery(id+"F5.wireOp",EDGE,"E5"),sQuery(id+"F11.wireOp",EDGE,"E130.0"),sQuery(id+"F11.wireOp",EDGE,"E133.MirrorCS")])]})});
            fillet(context, id + "F14", {"entities" : qUnion([Q0, Q1, Q2, Q3, Q4, Q5, Q6, Q7, Q8, Q9, Q10, Q11]), "radius" : 3.17 * mm, "tangentPropagation" : true, "allowEdgeOverflow" : false});
        }
        {
            var Q0;
            Q0=makeQuery(id+"F6.opExtrude","SWEPT_EDGE",EDGE,{"disambiguationData":[OSD([sQuery(id+"F5.wireOp",EDGE,"E5"),sQuery(id+"F5.wireOp",EDGE,"E8")])]});
            chamfer(context, id + "F15", {"entities" : qUnion([Q0]), "width" : 1.27 * mm, "tangentPropagation" : true});
        }
        {
            var Q0;
            Q0=makeQuery(id+"F6.opExtrude","SWEPT_FACE",FACE,{"disambiguationData":[OSD([sQuery(id+"F5.wireOp",EDGE,"E8")])]});
            var sketch = newSketch(context, id + "F16", { "sketchPlane" : qUnion([Q0])});
            skLineSegment(sketch, "E141", {"start": v(-219.08, 8.26) * mm, "end": v(-219.08, -4.44) * mm});
            skLineSegment(sketch, "E142.bottom", {"start": v(-219.08, -4.44) * mm, "end": v(219.08, -4.44) * mm});
            skLineSegment(sketch, "E142.top", {"start": v(-219.08, -9.53) * mm, "end": v(219.08, -9.53) * mm});
            skLineSegment(sketch, "E142.left", {"start": v(-219.08, -4.44) * mm, "end": v(-219.08, -9.53) * mm});
            skLineSegment(sketch, "E142.right", {"start": v(219.08, -4.44) * mm, "end": v(219.08, -9.53) * mm});
            skSolve(sketch);
        }
        {
            var Q0;
            Q0 = qSketchRegion(id + "F16", true);
            extrude(context, id + "F17", {"entities" : qUnion([Q0]), "operationType" : NewBodyOperationType.REMOVE, "oppositeDirection" : true, "depth" : 25.4 * mm, "offsetDistance" : 25.4 * mm});
        }
    });
